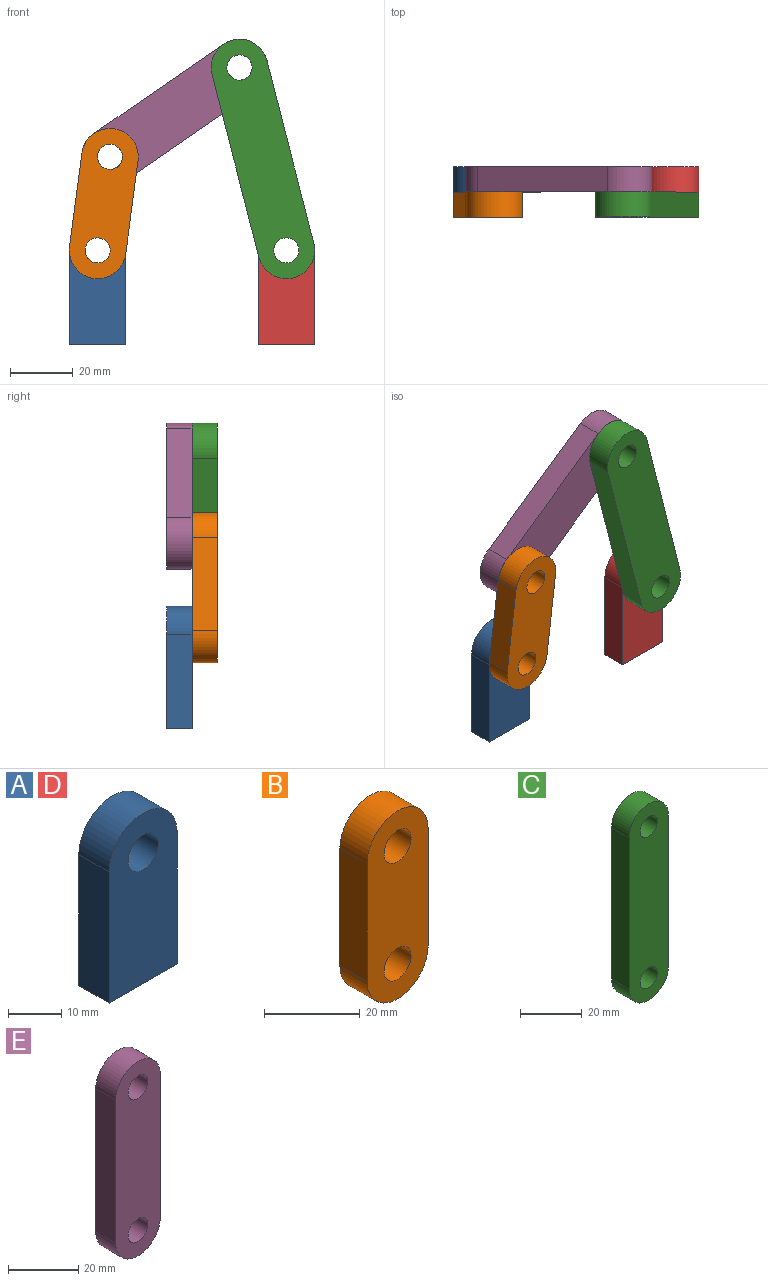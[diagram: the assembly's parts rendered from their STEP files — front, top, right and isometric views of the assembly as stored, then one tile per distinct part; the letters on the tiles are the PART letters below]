
ASSEMBLY  parts=5 mates=8
PART A: 7 faces, bbox 18x8x39 mm
  f0: plane 30x8mm, normal (1,0,0), area 240mm2, adj f1,f4,f5,f6
  f1: cylinder r=9mm len=18mm, axis (0,1,0), area 226.2mm2, adj f0,f2,f5,f6
  f2: plane 30x8mm, normal (-1,0,0), area 240mm2, adj f1,f4,f5,f6
  f3: cylinder r=4mm len=8mm, axis (0,1,0), area 201.1mm2, adj f5,f6
  f4: plane 18x8mm, normal (0,0,-1), area 144mm2, adj f0,f2,f5,f6
  f5: plane 39x18mm, normal (0,-1,0), area 617mm2, adj f0,f1,f2,f3,f4
  f6: plane 39x18mm, normal (0,1,0), area 617mm2, adj f0,f1,f2,f3,f4
PART B: 8 faces, bbox 18x8x48 mm
  f0: cylinder r=9mm len=18mm, axis (0,1,0), area 226.2mm2, adj f1,f5,f6,f7
  f1: plane 30x8mm, normal (-1,0,0), area 240mm2, adj f0,f2,f6,f7
  f2: cylinder r=9mm len=18mm, axis (0,1,0), area 226.2mm2, adj f1,f5,f6,f7
  f3: cylinder r=4mm len=8mm, axis (0,1,0), area 201.1mm2, adj f6,f7
  f4: cylinder r=4mm len=8mm, axis (0,1,0), area 201.1mm2, adj f6,f7
  f5: plane 30x8mm, normal (1,0,0), area 240mm2, adj f0,f2,f6,f7
  f6: plane 48x18mm, normal (0,-1,0), area 693.9mm2, adj f0,f1,f2,f3,f4,f5
  f7: plane 48x18mm, normal (0,1,0), area 693.9mm2, adj f0,f1,f2,f3,f4,f5
PART C: 8 faces, bbox 18x8x78 mm
  f0: cylinder r=9mm len=18mm, axis (0,1,0), area 226.2mm2, adj f1,f5,f6,f7
  f1: plane 60x8mm, normal (-1,0,0), area 480mm2, adj f0,f2,f6,f7
  f2: cylinder r=9mm len=18mm, axis (0,1,0), area 226.2mm2, adj f1,f5,f6,f7
  f3: cylinder r=4mm len=8mm, axis (0,1,0), area 201.1mm2, adj f6,f7
  f4: cylinder r=4mm len=8mm, axis (0,1,0), area 201.1mm2, adj f6,f7
  f5: plane 60x8mm, normal (1,0,0), area 480mm2, adj f0,f2,f6,f7
  f6: plane 78x18mm, normal (0,-1,0), area 1233.9mm2, adj f0,f1,f2,f3,f4,f5
  f7: plane 78x18mm, normal (0,1,0), area 1233.9mm2, adj f0,f1,f2,f3,f4,f5
PART D: same geometry as A
PART E: 8 faces, bbox 18x8x68 mm
  f0: cylinder r=9mm len=18mm, axis (0,1,0), area 226.2mm2, adj f1,f5,f6,f7
  f1: plane 50x8mm, normal (-1,0,0), area 400mm2, adj f0,f2,f6,f7
  f2: cylinder r=9mm len=18mm, axis (0,1,0), area 226.2mm2, adj f1,f5,f6,f7
  f3: cylinder r=4mm len=8mm, axis (0,1,0), area 201.1mm2, adj f6,f7
  f4: cylinder r=4mm len=8mm, axis (0,1,0), area 201.1mm2, adj f6,f7
  f5: plane 50x8mm, normal (1,0,0), area 400mm2, adj f0,f2,f6,f7
  f6: plane 68x18mm, normal (0,-1,0), area 1053.9mm2, adj f0,f1,f2,f3,f4,f5
  f7: plane 68x18mm, normal (0,1,0), area 1053.9mm2, adj f0,f1,f2,f3,f4,f5
PLACE A t=(-62.09,3.94,-24.44)mm fixed
PLACE B rot(axis=(0,1,0),7.5deg) t=(-180.16,-4.06,10.98)mm
PLACE C rot(axis=(0,-1,0),14.4deg) t=(-79.11,-4.06,5.56)mm
PLACE D t=(-2.09,3.94,-24.44)mm fixed
PLACE E rot(axis=(0,1,0),55.4deg) t=(-114.4,3.94,5.16)mm
MATE revolute C.f2 <-> D.f1  axis (0,1,0) through (-79.11,-4.06,5.56)mm
MATE revolute B.f0 <-> E.f2  axis (0,1,0) through (-135.18,-4.06,35.3)mm
MATE planar B.f7 <-> E.f6  axis (0,1,0) through (-137.15,-4.06,20.43)mm
MATE parallel D.f4 <-> A.f4  axis (0,0,-1) through (-79.11,-0.06,-24.44)mm
MATE revolute A.f1 <-> B.f2  axis (0,-1,0) through (-139.11,-4.06,5.56)mm
MATE revolute C.f0 <-> E.f0  axis (0,1,0) through (-94.02,-4.06,63.68)mm
MATE planar B.f7 <-> A.f5  axis (0,1,0) through (-137.15,-4.06,20.43)mm
MATE parallel A.f0 <-> D.f2  axis (1,0,0) through (-130.11,-0.06,-9.44)mm
